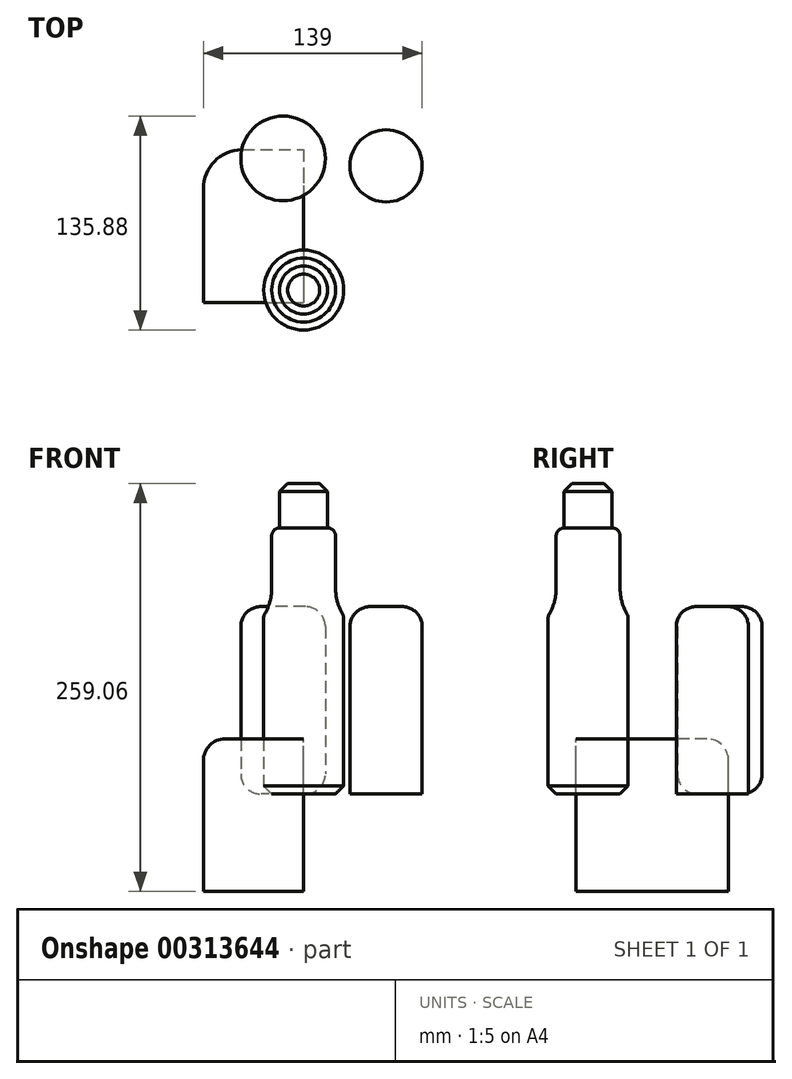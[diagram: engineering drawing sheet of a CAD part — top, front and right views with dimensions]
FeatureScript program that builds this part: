
annotation { "Feature Type Name" : "Feature", "Feature Type Description" : "" }
export const myFeature = defineFeature(function(context is Context, id is Id, definition is map)
    precondition{}
    {
        {
            var Q0;
            Q0=qCreatedBy(makeId("Top.planeOp"),FACE);
            var sketch = newSketch(context, id + "F0", { "sketchPlane" : qUnion([Q0])});
            skCircle(sketch, "E0", {"center": v(0, -42.39) * mm, "radius": 25.39 * mm});
            skCircle(sketch, "E1", {"center": v(-13.03, 41.24) * mm, "radius": 26.87 * mm});
            skCircle(sketch, "E2", {"center": v(52.38, 36.5) * mm, "radius": 22.93 * mm});
            skSolve(sketch);
        }
        {
            var Q0;
            Q0 = qSketchRegion(id + "F0", true);
            extrude(context, id + "F1", {"entities" : qUnion([Q0]), "depth" : 119 * mm});
        }
        {
            var Q0;
            Q0=makeQuery(id+"F1.opExtrude","CAP_EDGE",EDGE,{"disambiguationData":[OSD([sQuery(id+"F0.wireOp",EDGE,"E0")])],"isStart":false});
            var Q1;
            Q1=makeQuery(id+"F1.opExtrude","SWEPT_FACE",FACE,{"disambiguationData":[OSD([sQuery(id+"F0.wireOp",EDGE,"E0")])]});
            chamfer(context, id + "F2", {"entities" : qUnion([Q0, Q1]), "width" : 5.08 * mm, "tangentPropagation" : true});
        }
        {
            var Q0;
            Q0=makeQuery(id+"F1.opExtrude","CAP_EDGE",EDGE,{"disambiguationData":[OSD([sQuery(id+"F0.wireOp",EDGE,"E2")])],"isStart":false});
            var Q1;
            Q1=makeQuery(id+"F1.opExtrude","SWEPT_FACE",FACE,{"disambiguationData":[OSD([sQuery(id+"F0.wireOp",EDGE,"E1")])]});
            fillet(context, id + "F3", {"entities" : qUnion([Q0, Q1]), "radius" : 12.7 * mm, "tangentPropagation" : true, "allowEdgeOverflow" : false});
        }
        {
            var Q0;
            Q0=makeQuery(id+"F1.opExtrude","CAP_FACE",FACE,{"disambiguationData":[OSD([sQuery(id+"F0.wireOp",EDGE,"E0")])],"isStart":false});
            extrude(context, id + "F4", {"entities" : qUnion([Q0]), "operationType" : NewBodyOperationType.ADD, "depth" : 49.98 * mm});
        }
        {
            var Q0;
            Q0=makeQuery(id+"F4.opExtrude","CAP_EDGE",EDGE,{"disambiguationData":[OSD([sQuery(id+"F0.wireOp",EDGE,"E0")])],"isStart":false});
            fillet(context, id + "F5", {"entities" : qUnion([Q0]), "radius" : 5.08 * mm, "tangentPropagation" : true, "allowEdgeOverflow" : false});
        }
        {
            var Q0;
            {var subQ0=sQuery(id+"F0.wireOp",EDGE,"E0");Q0=makeQuery(id+"F2.opChamfer","BLEND_EDGE",EDGE,{"blendedFrom":[makeQuery(id+"F1.opExtrude","CAP_EDGE",EDGE,{"disambiguationData":[OSD([subQ0])],"isStart":false}),makeQuery(id+"F1.opExtrude","SWEPT_FACE",FACE,{"disambiguationData":[OSD([subQ0])]})],"blendedInto":[makeQuery(id+"F1.opExtrude","SWEPT_FACE",FACE,{"disambiguationData":[OSD([subQ0])]})]});}
            fillet(context, id + "F6", {"entities" : qUnion([Q0]), "radius" : 5.08 * mm, "tangentPropagation" : true, "allowEdgeOverflow" : false});
        }
        {
            var Q0;
            {var subQ0=sQuery(id+"F0.wireOp",EDGE,"E0");Q0=makeQuery(id+"F4.boolean.opBoolean","MERGE",EDGE,{"derivedFrom":[makeQuery(id+"F2.opChamfer","BLEND_EDGE",EDGE,{"blendedFrom":[makeQuery(id+"F1.opExtrude","CAP_EDGE",EDGE,{"disambiguationData":[OSD([subQ0])],"isStart":false}),makeQuery(id+"F1.opExtrude","CAP_FACE",FACE,{"disambiguationData":[OSD([subQ0])],"isStart":false})],"blendedInto":[makeQuery(id+"F1.opExtrude","CAP_FACE",FACE,{"disambiguationData":[OSD([subQ0])],"isStart":false})]}),makeQuery(id+"F4.opExtrude","CAP_EDGE",EDGE,{"disambiguationData":[OSD([subQ0])],"isStart":true})]});}
            fillet(context, id + "F7", {"entities" : qUnion([Q0]), "radius" : 31.68 * mm, "tangentPropagation" : true, "allowEdgeOverflow" : false});
        }
        {
            var Q0;
            Q0=qCreatedBy(makeId("Top.planeOp"),FACE);
            var sketch = newSketch(context, id + "F8", { "sketchPlane" : qUnion([Q0])});
            skLineSegment(sketch, "E3.bottom", {"start": v(-15.16, 0) * mm, "end": v(-55.4, 0) * mm});
            skLineSegment(sketch, "E3.top", {"start": v(-15.16, -49.58) * mm, "end": v(-55.4, -49.58) * mm});
            skLineSegment(sketch, "E3.left", {"start": v(-15.16, 0) * mm, "end": v(-15.16, -49.58) * mm});
            skLineSegment(sketch, "E3.right", {"start": v(-55.4, 0) * mm, "end": v(-55.4, -49.58) * mm});
            skSolve(sketch);
        }
        {
            var Q0;
            Q0=qCreatedBy(makeId("Right.planeOp"),FACE);
            var sketch = newSketch(context, id + "F9", { "sketchPlane" : qUnion([Q0])});
            skLineSegment(sketch, "E4.bottom", {"start": v(46.86, -61.88) * mm, "end": v(-50.21, -61.88) * mm});
            skLineSegment(sketch, "E4.top", {"start": v(46.86, 34.97) * mm, "end": v(-50.21, 34.97) * mm});
            skLineSegment(sketch, "E4.left", {"start": v(46.86, -61.88) * mm, "end": v(46.86, 34.97) * mm});
            skLineSegment(sketch, "E4.right", {"start": v(-50.21, -61.88) * mm, "end": v(-50.21, 34.97) * mm});
            skSolve(sketch);
        }
        {
            var Q0;
            Q0 = qSketchRegion(id + "F9", true);
            extrude(context, id + "F10", {"entities" : qUnion([Q0]), "oppositeDirection" : true, "depth" : 63.69 * mm});
        }
        {
            var Q0;
            Q0=makeQuery(id+"F10.opExtrude","CAP_EDGE",EDGE,{"disambiguationData":[OSD([sQuery(id+"F9.wireOp",EDGE,"E4.left")])],"isStart":false});
            fillet(context, id + "F11", {"entities" : qUnion([Q0]), "radius" : 24.93 * mm, "tangentPropagation" : true, "allowEdgeOverflow" : false});
        }
        {
            var Q0;
            Q0=makeQuery(id+"F10.opExtrude","CAP_EDGE",EDGE,{"disambiguationData":[OSD([sQuery(id+"F9.wireOp",EDGE,"E4.top")])],"isStart":false});
            var Q1;
            Q1=makeQuery(id+"F11.opFillet","BLEND_EDGE",EDGE,{"blendedFrom":[makeQuery(id+"F10.opExtrude","CAP_EDGE",EDGE,{"disambiguationData":[OSD([sQuery(id+"F9.wireOp",EDGE,"E4.left")])],"isStart":false}),makeQuery(id+"F10.opExtrude","SWEPT_FACE",FACE,{"disambiguationData":[OSD([sQuery(id+"F9.wireOp",EDGE,"E4.top")])]})],"blendedInto":[makeQuery(id+"F10.opExtrude","SWEPT_FACE",FACE,{"disambiguationData":[OSD([sQuery(id+"F9.wireOp",EDGE,"E4.top")])]})]});
            fillet(context, id + "F12", {"entities" : qUnion([Q0, Q1]), "radius" : 13.86 * mm, "tangentPropagation" : true, "allowEdgeOverflow" : false});
        }
        {
            var Q0;
            Q0=makeQuery(id+"F4.opExtrude","CAP_FACE",FACE,{"disambiguationData":[OSD([sQuery(id+"F0.wireOp",EDGE,"E0")])],"isStart":false});
            extrude(context, id + "F13", {"entities" : qUnion([Q0]), "operationType" : NewBodyOperationType.ADD, "depth" : 28.2 * mm});
        }
        {
            var Q0;
            Q0=makeQuery(id+"F1.opExtrude","SWEPT_FACE",FACE,{"disambiguationData":[OSD([sQuery(id+"F0.wireOp",EDGE,"E1")])]});
            var Q1;
            Q1=makeQuery(id+"F13.opExtrude","CAP_EDGE",EDGE,{"disambiguationData":[OSD([sQuery(id+"F0.wireOp",EDGE,"E0")])],"isStart":false});
            var Q2;
            {var subQ0=sQuery(id+"F0.wireOp",EDGE,"E1");Q2=makeQuery(id+"F3.opFillet","BLEND_FACE",FACE,{"disambiguationData":[OSD([subQ0]),TDD([makeQuery(id+"F1.opExtrude","CAP_EDGE",EDGE,{"disambiguationData":[OSD([subQ0])],"isStart":false})])]});}
            var Q3;
            Q3=makeQuery(id+"F4.opExtrude","SWEPT_FACE",FACE,{"disambiguationData":[OSD([sQuery(id+"F0.wireOp",EDGE,"E0")])]});
            chamfer(context, id + "F14", {"entities" : qUnion([Q0, Q1, Q2, Q3]), "width" : 5.08 * mm, "tangentPropagation" : true});
        }
    });
